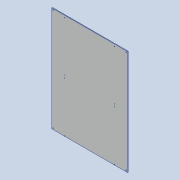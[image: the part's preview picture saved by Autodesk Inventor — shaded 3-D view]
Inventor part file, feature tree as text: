
AUTODESK INVENTOR PART (.ipt)
format: ipt  version: 2020 (Build 240168000, 168)  size: 129,536 bytes
history: native  units: mm
features: reference x8, other x4, sketch x3, extrude x2, hole x1
ambient origin geometry x8: Origin, YZ Plane, XZ Plane, XY Plane, X Axis, Y Axis, Z Axis, Center Point
bodies: Solid1 (feature_tree)
feature tree (18):
  extrude  "Extrusion1"  Depth=317.0mm
  extrude  "Extrusion2"  Depth=5.0mm
  hole  "Hole1"  [1 undecoded]
  sketch  "Sketch1"  dims[d0=440.0mm d1=317.0mm]
  sketch  "Sketch2"  dims[d3=5.0mm d4=5.0mm]
  sketch  "Sketch3"  dims[d5=4.0mm d6=3.0mm d7=0.0mm d8=3.0mm d9=2.0mm d10=0.0mm d11=2.5mm d12=6.0mm d13=4.0mm d14=2.0mm d15=90.0deg d16=8.8mm d17=20.594885mm]
  reference  "Reference1"
  reference  "Reference2"
  reference  "Reference3"
  reference  "Reference4"
  reference  "Reference5"
  reference  "Reference6"
  reference  "Reference7"
  reference  "Reference8"
  parser-record x1  (decoder bookkeeping rows leaked as tree rows — omitted from the tree; the rows remain in map.json)
  other  "0008-10-03 YAxis.iam"
  other  "0008-20-1007 HEATING BED.ipt:35"
  other  "0008-20-1007 HEATING BED.ipt:36"
note: 1 required parameter value undecoded (feature->parameter linkage not recoverable at this tier; creation-order binding heuristic only, values carry confidence <= 0.55)
note: 1 file-system path scrubbed to <path> (originals preserved in map.json)
